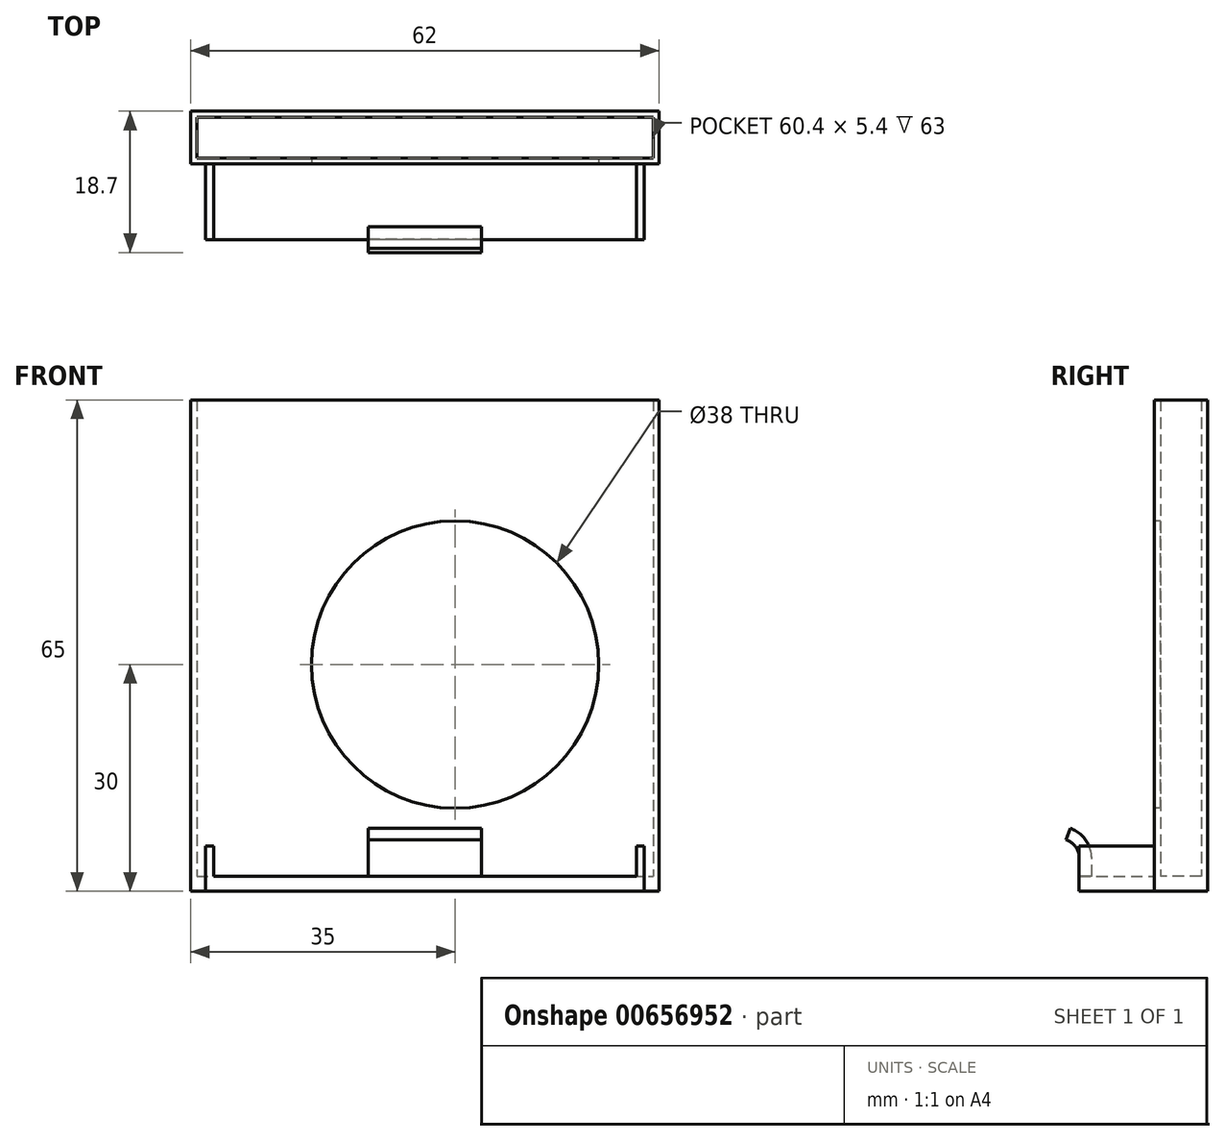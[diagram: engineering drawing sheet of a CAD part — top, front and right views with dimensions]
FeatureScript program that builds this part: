
annotation { "Feature Type Name" : "Feature", "Feature Type Description" : "" }
export const myFeature = defineFeature(function(context is Context, id is Id, definition is map)
    precondition{}
    {
        {
            var Q0;
            Q0=qCreatedBy(makeId("Top.planeOp"),FACE);
            var sketch = newSketch(context, id + "F0", { "sketchPlane" : qUnion([Q0])});
            skLineSegment(sketch, "E0.bottom", {"start": v(31, -3.5) * mm, "end": v(-31, -3.5) * mm});
            skLineSegment(sketch, "E0.top", {"start": v(31, 3.5) * mm, "end": v(-31, 3.5) * mm});
            skLineSegment(sketch, "E0.left", {"start": v(31, -3.5) * mm, "end": v(31, 3.5) * mm});
            skLineSegment(sketch, "E0.right", {"start": v(-31, -3.5) * mm, "end": v(-31, 3.5) * mm});
            skPoint(sketch, "E0.middle", {"position": v(0, 0) * mm});
            skLineSegment(sketch, "E1.0", {"start": v(30.2, 2.7) * mm, "end": v(-30.2, 2.7) * mm});
            skLineSegment(sketch, "E1.1", {"start": v(30.2, -2.7) * mm, "end": v(30.2, 2.7) * mm});
            skLineSegment(sketch, "E1.2", {"start": v(30.2, -2.7) * mm, "end": v(-30.2, -2.7) * mm});
            skLineSegment(sketch, "E1.3", {"start": v(-30.2, -2.7) * mm, "end": v(-30.2, 2.7) * mm});
            skLineSegment(sketch, "E2.bottom", {"start": v(29, -3.5) * mm, "end": v(-29, -3.5) * mm});
            skLineSegment(sketch, "E2.top", {"start": v(29, -13.5) * mm, "end": v(-29, -13.5) * mm});
            skLineSegment(sketch, "E2.left", {"start": v(29, -3.5) * mm, "end": v(29, -13.5) * mm});
            skLineSegment(sketch, "E2.right", {"start": v(-29, -3.5) * mm, "end": v(-29, -13.5) * mm});
            skPoint(sketch, "E2.middle", {"position": v(0, -8.5) * mm});
            skLineSegment(sketch, "E3", {"start": v(-27.97, -3.5) * mm, "end": v(-27.97, -13.5) * mm});
            skLineSegment(sketch, "E4.MirrorCS", {"start": v(27.97, -3.5) * mm, "end": v(27.97, -13.5) * mm});
            skLineSegment(sketch, "E5.bottom", {"start": v(5, -13.5) * mm, "end": v(-5, -13.5) * mm});
            skLineSegment(sketch, "E5.top", {"start": v(5, -21.5) * mm, "end": v(-5, -21.5) * mm});
            skLineSegment(sketch, "E5.left", {"start": v(5, -13.5) * mm, "end": v(5, -21.5) * mm});
            skLineSegment(sketch, "E5.right", {"start": v(-5, -13.5) * mm, "end": v(-5, -21.5) * mm});
            skPoint(sketch, "E5.middle", {"position": v(0, -17.5) * mm});
            skPoint(sketch, "E5.middle.positionSnap0", {"position": v(0, -13.5) * mm});
            skPoint(sketch, "E5.centerSnap0", {"position": v(0, -13.5) * mm});
            skCircle(sketch, "E6", {"center": v(-2.13, -17.5) * mm, "radius": 1.5 * mm});
            skSolve(sketch);
        }
        {
            var Q0;
            Q0=makeQuery(id+"F0.imprint","IMPRINT",FACE,{"disambiguationData":[TD([[makeQuery(id+"F0.imprint","IMPRINT",EDGE,{"derivedFrom":sQuery(id+"F0.wireOp",EDGE,"E1.0")}),1.0]])]});
            var Q1;
            Q1=makeQuery(id+"F0.imprint","IMPRINT",FACE,{"disambiguationData":[TD([[makeQuery(id+"F0.imprint","IMPRINT",EDGE,{"derivedFrom":sQuery(id+"F0.wireOp",EDGE,"E0.bottom")}),-1.0]])]});
            var Q2;
            {var subQ0=sQuery(id+"F0.wireOp",EDGE,"E3");Q2=makeQuery(id+"F0.imprint","IMPRINT",FACE,{"disambiguationData":[TD([[makeQuery(id+"F0.imprint","IMPRINT",EDGE,{"derivedFrom":subQ0}),1.0]])]});}
            var Q3;
            {var subQ0=sQuery(id+"F0.wireOp",EDGE,"E2.right");Q3=makeQuery(id+"F0.imprint","IMPRINT",FACE,{"disambiguationData":[TD([[makeQuery(id+"F0.imprint","IMPRINT",EDGE,{"derivedFrom":subQ0}),1.0]])]});}
            var Q4;
            {var subQ0=sQuery(id+"F0.wireOp",EDGE,"E2.left");Q4=makeQuery(id+"F0.imprint","IMPRINT",FACE,{"disambiguationData":[TD([[makeQuery(id+"F0.imprint","IMPRINT",EDGE,{"derivedFrom":subQ0}),-1.0]])]});}
            var Q5;
            Q5=makeQuery(id+"F0.imprint","IMPRINT",FACE,{"disambiguationData":[TD([[makeQuery(id+"F0.imprint","IMPRINT",EDGE,{"derivedFrom":sQuery(id+"F0.wireOp",EDGE,"E5.bottom")}),1.0]])]});
            extrude(context, id + "F1", {"entities" : qUnion([Q0, Q1, Q2, Q3, Q4, Q5]), "depth" : 2 * mm, "offsetDistance" : 25 * mm});
        }
        {
            var Q0;
            Q0=makeQuery(id+"F0.imprint","IMPRINT",FACE,{"disambiguationData":[TD([[makeQuery(id+"F0.imprint","IMPRINT",EDGE,{"derivedFrom":sQuery(id+"F0.wireOp",EDGE,"E0.bottom")}),-1.0]])]});
            extrude(context, id + "F2", {"entities" : qUnion([Q0]), "operationType" : NewBodyOperationType.ADD, "depth" : 65 * mm, "offsetDistance" : 25 * mm});
        }
        {
            var Q0;
            {var subQ0=sQuery(id+"F0.wireOp",EDGE,"E0.bottom");Q0=makeQuery(id+"F2.boolean.opBoolean","MERGE",FACE,{"derivedFrom":[makeQuery(id+"F1.opExtrude","SWEPT_FACE",FACE,{"disambiguationData":[OSD([subQ0])]}),makeQuery(id+"F2.opExtrude","SWEPT_FACE",FACE,{"disambiguationData":[OSD([subQ0])]})]});}
            var sketch = newSketch(context, id + "F3", { "sketchPlane" : qUnion([Q0])});
            skLineSegment(sketch, "E7", {"start": v(4, 66.85) * mm, "end": v(4, -3.45) * mm, "construction": true});
            skLineSegment(sketch, "E8", {"start": v(-46.38, 30) * mm, "end": v(43.3, 30) * mm, "construction": true});
            skCircle(sketch, "E9", {"center": v(4, 30) * mm, "radius": 19 * mm});
            skSolve(sketch);
        }
        {
            var Q0;
            Q0=makeQuery(id+"F3.imprint","IMPRINT",FACE,{"disambiguationData":[TD([[makeQuery(id+"F3.imprint","IMPRINT",EDGE,{"derivedFrom":sQuery(id+"F3.wireOp",EDGE,"E9")}),1.0]])]});
            extrude(context, id + "F4", {"entities" : qUnion([Q0]), "operationType" : NewBodyOperationType.REMOVE, "oppositeDirection" : true, "depth" : 2 * mm, "offsetDistance" : 25 * mm});
        }
        {
            var Q0;
            {var subQ0=sQuery(id+"F0.wireOp",EDGE,"E2.left");Q0=makeQuery(id+"F0.imprint","IMPRINT",FACE,{"disambiguationData":[TD([[makeQuery(id+"F0.imprint","IMPRINT",EDGE,{"derivedFrom":subQ0}),-1.0]])]});}
            var Q1;
            {var subQ0=sQuery(id+"F0.wireOp",EDGE,"E2.right");Q1=makeQuery(id+"F0.imprint","IMPRINT",FACE,{"disambiguationData":[TD([[makeQuery(id+"F0.imprint","IMPRINT",EDGE,{"derivedFrom":subQ0}),1.0]])]});}
            extrude(context, id + "F5", {"entities" : qUnion([Q0, Q1]), "operationType" : NewBodyOperationType.ADD, "depth" : 6 * mm, "offsetDistance" : 25 * mm});
        }
        {
            var Q0;
            {var subQ0=sQuery(id+"F0.wireOp",EDGE,"E5.right");var subQ1=sQuery(id+"F0.wireOp",EDGE,"E5.left");var subQ2=sQuery(id+"F0.wireOp",EDGE,"E2.right");var subQ3=sQuery(id+"F0.wireOp",EDGE,"E2.left");var subQ4=sQuery(id+"F0.wireOp",EDGE,"E5.top");var subQ6=sQuery(id+"F0.wireOp",EDGE,"E0.bottom");var subQ7=sQuery(id+"F0.wireOp",EDGE,"E0.left");var subQ8=sQuery(id+"F0.wireOp",EDGE,"E6");var subQ9=sQuery(id+"F0.wireOp",EDGE,"E0.right");var subQ10=sQuery(id+"F0.wireOp",EDGE,"E2.top");Q0=makeQuery(id+"F2.boolean.opBoolean","SPLIT",FACE,{"disambiguationData":[TD([makeQuery(id+"F1.opExtrude","SWEPT_FACE",FACE,{"disambiguationData":[OSD([subQ3])]})])],"derivedFrom":makeQuery(id+"F1.opExtrude","CAP_FACE",FACE,{"disambiguationData":[OSD([subQ6,sQuery(id+"F0.wireOp",EDGE,"E0.top"),subQ7,subQ9,subQ10,subQ3,subQ2,subQ4,subQ1,subQ0,subQ8])],"isStart":false})});}
            var sketch = newSketch(context, id + "F6", { "sketchPlane" : qUnion([Q0])});
            skLineSegment(sketch, "E10.bottom", {"start": v(7.5, -13.4) * mm, "end": v(-7.5, -13.4) * mm});
            skLineSegment(sketch, "E10.top", {"start": v(7.5, -11.8) * mm, "end": v(-7.5, -11.8) * mm});
            skLineSegment(sketch, "E10.left", {"start": v(7.5, -13.4) * mm, "end": v(7.5, -11.8) * mm});
            skLineSegment(sketch, "E10.right", {"start": v(-7.5, -13.4) * mm, "end": v(-7.5, -11.8) * mm});
            skPoint(sketch, "E10.middle", {"position": v(0, -12.6) * mm});
            skSolve(sketch);
        }
        {
            var Q0;
            Q0=qCreatedBy(makeId("Right.planeOp"),FACE);
            var sketch = newSketch(context, id + "F7", { "sketchPlane" : qUnion([Q0])});
            skLineSegment(sketch, "E11", {"start": v(-13.62, 1.5) * mm, "end": v(-13.62, 4.3) * mm});
            skArc(sketch, "E12", {"start": v(-13.62, 4.3) * mm, "mid": v(-14.07, 5.73) * mm, "end": v(-15.27, 6.63) * mm});
            skSolve(sketch);
        }
        {
            var Q0;
            Q0 = qSketchRegion(id + "F6", true);
            var Q1;
            Q1 = qConstructionFilter(qBodyType(qCreatedBy(id + "F7" ,EDGE), BodyType.WIRE), ConstructionObject.NO);
            sweep(context, id + "F8", {"operationType" : NewBodyOperationType.ADD, "profiles" : qUnion([Q0]), "path" : qUnion([Q1])});
        }
    });
